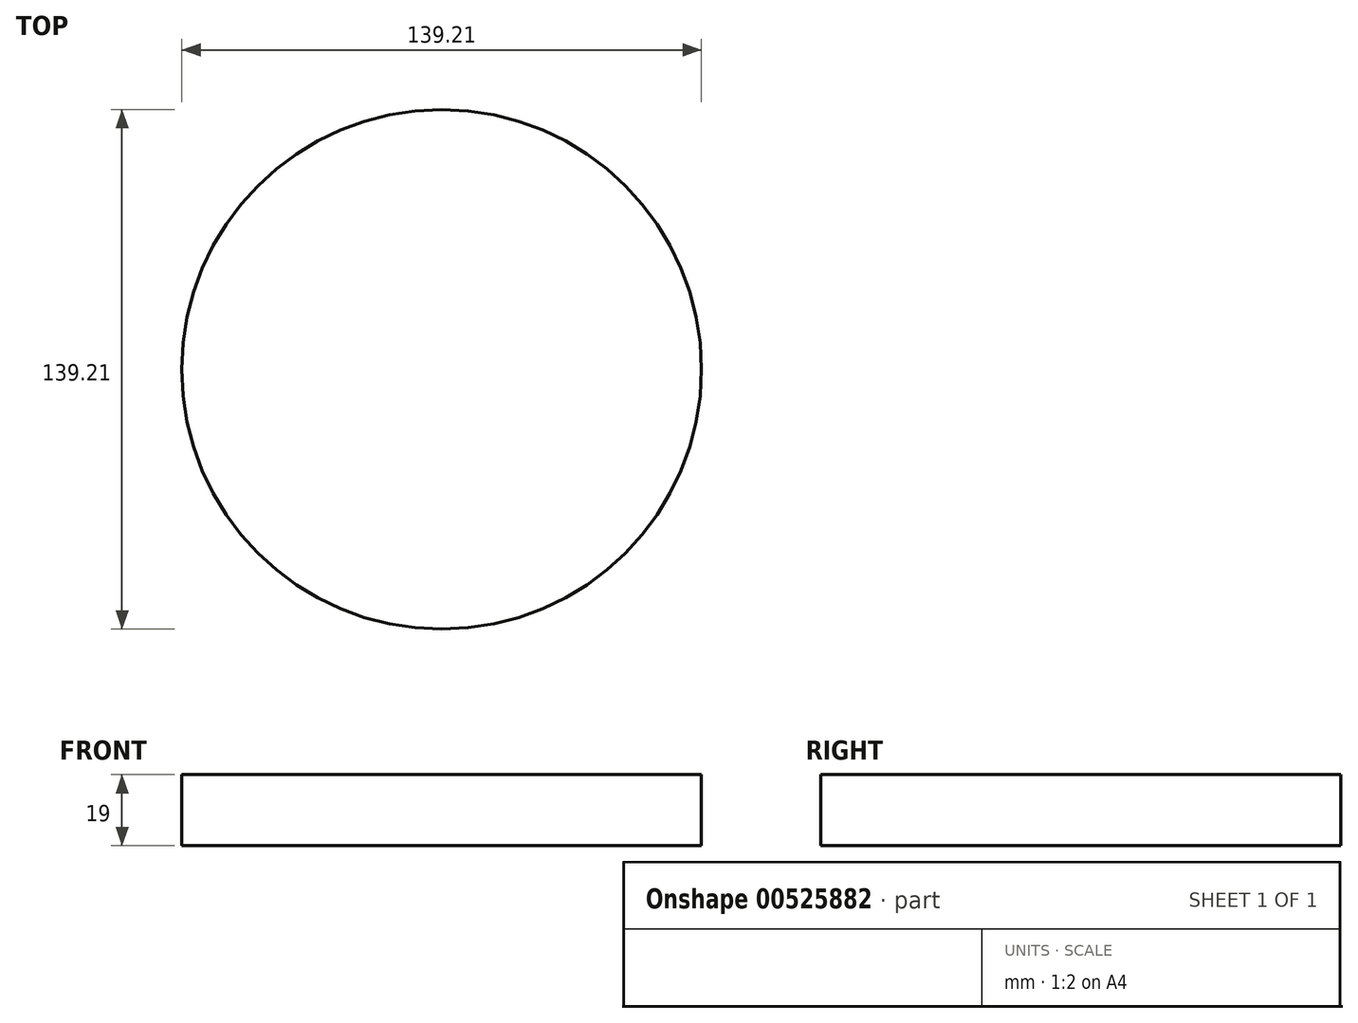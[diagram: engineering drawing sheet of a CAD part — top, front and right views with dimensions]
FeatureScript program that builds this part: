
annotation { "Feature Type Name" : "Feature", "Feature Type Description" : "" }
export const myFeature = defineFeature(function(context is Context, id is Id, definition is map)
    precondition{}
    {
        {
            var Q0;
            Q0=qCreatedBy(makeId("Top.planeOp"),FACE);
            var sketch = newSketch(context, id + "F0", { "sketchPlane" : qUnion([Q0])});
            skCircle(sketch, "E0", {"center": v(0.1, -1.53) * mm, "radius": 69.6 * mm});
            skSolve(sketch);
        }
        {
            var Q0;
            Q0 = qSketchRegion(id + "F0", true);
            extrude(context, id + "F1", {"entities" : qUnion([Q0]), "depth" : 19 * mm, "offsetDistance" : 25.4 * mm});
        }
    });
